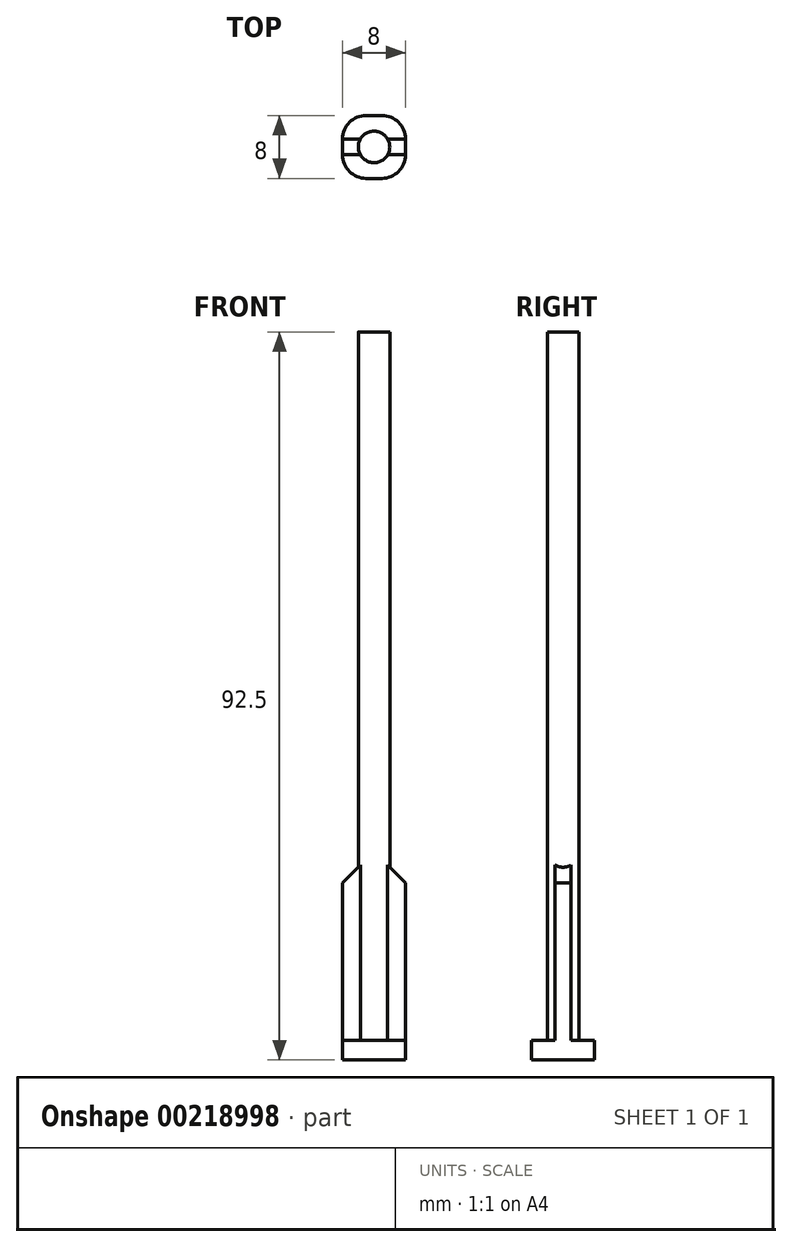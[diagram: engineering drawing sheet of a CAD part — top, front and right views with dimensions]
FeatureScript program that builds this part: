
annotation { "Feature Type Name" : "Feature", "Feature Type Description" : "" }
export const myFeature = defineFeature(function(context is Context, id is Id, definition is map)
    precondition{}
    {
        {
            var Q0;
            Q0=qCreatedBy(makeId("Top.planeOp"),FACE);
            var sketch = newSketch(context, id + "F0", { "sketchPlane" : qUnion([Q0])});
            skLineSegment(sketch, "E0.bottom", {"start": v(-15.37, 11.88) * mm, "end": v(-7.37, 11.88) * mm});
            skLineSegment(sketch, "E0.top", {"start": v(-15.37, 3.88) * mm, "end": v(-7.37, 3.88) * mm});
            skLineSegment(sketch, "E0.left", {"start": v(-15.37, 11.88) * mm, "end": v(-15.37, 3.88) * mm});
            skLineSegment(sketch, "E0.right", {"start": v(-7.37, 11.88) * mm, "end": v(-7.37, 3.88) * mm});
            skSolve(sketch);
        }
        {
            var Q0;
            Q0 = qSketchRegion(id + "F0", true);
            extrude(context, id + "F1", {"entities" : qUnion([Q0]), "depth" : 2.5 * mm});
        }
        {
            var Q0;
            Q0=makeQuery(id+"F1.opExtrude","SWEPT_EDGE",EDGE,{"disambiguationData":[OSD([sQuery(id+"F0.wireOp",EDGE,"E0.top"),sQuery(id+"F0.wireOp",EDGE,"E0.left")])]});
            var Q1;
            Q1=makeQuery(id+"F1.opExtrude","SWEPT_EDGE",EDGE,{"disambiguationData":[OSD([sQuery(id+"F0.wireOp",EDGE,"E0.bottom"),sQuery(id+"F0.wireOp",EDGE,"E0.left")])]});
            var Q2;
            Q2=makeQuery(id+"F1.opExtrude","SWEPT_EDGE",EDGE,{"disambiguationData":[OSD([sQuery(id+"F0.wireOp",EDGE,"E0.top"),sQuery(id+"F0.wireOp",EDGE,"E0.right")])]});
            var Q3;
            Q3=makeQuery(id+"F1.opExtrude","SWEPT_EDGE",EDGE,{"disambiguationData":[OSD([sQuery(id+"F0.wireOp",EDGE,"E0.bottom"),sQuery(id+"F0.wireOp",EDGE,"E0.right")])]});
            fillet(context, id + "F2", {"entities" : qUnion([Q0, Q1, Q2, Q3]), "radius" : 3 * mm, "tangentPropagation" : true, "allowEdgeOverflow" : false});
        }
        {
            var Q0;
            Q0=makeQuery(id+"F1.opExtrude","CAP_FACE",FACE,{"disambiguationData":[OSD([sQuery(id+"F0.wireOp",EDGE,"E0.bottom"),sQuery(id+"F0.wireOp",EDGE,"E0.top"),sQuery(id+"F0.wireOp",EDGE,"E0.left"),sQuery(id+"F0.wireOp",EDGE,"E0.right")])],"isStart":false});
            var sketch = newSketch(context, id + "F3", { "sketchPlane" : qUnion([Q0])});
            skCircle(sketch, "E1", {"center": v(-11.37, 7.88) * mm, "radius": 2 * mm});
            skSolve(sketch);
        }
        {
            var Q0;
            Q0 = qSketchRegion(id + "F3", true);
            extrude(context, id + "F4", {"entities" : qUnion([Q0]), "operationType" : NewBodyOperationType.ADD, "depth" : 90 * mm});
        }
        {
            var Q0;
            Q0=makeQuery(id+"F1.opExtrude","CAP_FACE",FACE,{"disambiguationData":[OSD([sQuery(id+"F0.wireOp",EDGE,"E0.bottom"),sQuery(id+"F0.wireOp",EDGE,"E0.top"),sQuery(id+"F0.wireOp",EDGE,"E0.left"),sQuery(id+"F0.wireOp",EDGE,"E0.right")])],"isStart":false});
            var sketch = newSketch(context, id + "F5", { "sketchPlane" : qUnion([Q0])});
            skLineSegment(sketch, "E2.bottom", {"start": v(-15.37, 8.88) * mm, "end": v(-7.37, 8.88) * mm});
            skLineSegment(sketch, "E2.top", {"start": v(-15.37, 6.88) * mm, "end": v(-7.37, 6.88) * mm});
            skLineSegment(sketch, "E2.left", {"start": v(-15.37, 8.88) * mm, "end": v(-15.37, 6.88) * mm});
            skLineSegment(sketch, "E2.right", {"start": v(-7.37, 8.88) * mm, "end": v(-7.37, 6.88) * mm});
            skSolve(sketch);
        }
        {
            var Q0;
            Q0 = qSketchRegion(id + "F5", true);
            extrude(context, id + "F6", {"entities" : qUnion([Q0]), "operationType" : NewBodyOperationType.ADD, "depth" : 25 * mm});
        }
        {
            var Q0;
            Q0=makeQuery(id+"F6.opExtrude","CAP_EDGE",EDGE,{"disambiguationData":[OSD([sQuery(id+"F5.wireOp",EDGE,"E2.left")])],"isStart":false});
            var Q1;
            Q1=makeQuery(id+"F6.opExtrude","CAP_EDGE",EDGE,{"disambiguationData":[OSD([sQuery(id+"F5.wireOp",EDGE,"E2.right")])],"isStart":false});
            chamfer(context, id + "F7", {"entities" : qUnion([Q0, Q1]), "width" : 5 * mm, "tangentPropagation" : true});
        }
    });
